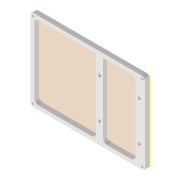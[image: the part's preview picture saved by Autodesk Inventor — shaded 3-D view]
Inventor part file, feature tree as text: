
AUTODESK INVENTOR PART (.ipt)
format: ipt  version: 2022 (Build 260153000, 153)  size: 550,912 bytes
history: native  units: mm
features: sketch x4, extrude x3, other x3, reference x2, projected_geometry x2, plane x1, hole x1, fillet x1
ambient origin geometry x8: Origin, YZ Plane, XZ Plane, XY Plane, X Axis, Y Axis, Z Axis, Center Point
bodies: Volumenkörper1 (feature_tree)
feature tree (17):
  plane  "Arbeitsebene1"
  extrude  "Extrusion1"  Depth=1.0mm TaperAngle=0.0deg
  extrude  "Extrusion2"  Depth=50.0mm
  hole  "Bohrung1"  [1 undecoded]
  extrude  "Extrusion3"  Depth=5.0mm
  fillet  "Rundung1"  Radius=18.0mm
  sketch  "Skizze1"  dims[d0=0.5mm d1=1.0mm d2=0.0mm]
  reference  "Referenz1"
  reference  "Referenz2"
  sketch  "Skizze2"  dims[d3=5.0mm d4=0.0mm d5=50.0mm]
  projected_geometry  "Projizierte Kontur1"
  sketch  "Skizze3"  dims[d6=50.0mm d7=40.0mm]
  sketch  "Skizze4"  dims[d8=4.0mm d9=6.0mm d10=4.0mm d11=2.0mm d12=90.0deg d13=8.0mm d14=20.594885mm d15=5.0mm d17=18.0mm d19=5.0mm d24=0.0mm d25=0.0mm d26=4.5mm d27=4.5mm d28=4.5mm d29=5.0mm]
  projected_geometry  "Projizierte Kontur2"
  other  "Omnicscope_Xiao.iam"
  other  "00_Omniscope_PCB_USBC:1"
  other  "Omniscope_USBC_Base_Top+:1"
note: 1 required parameter value undecoded (feature->parameter linkage not recoverable at this tier; creation-order binding heuristic only, values carry confidence <= 0.55)
